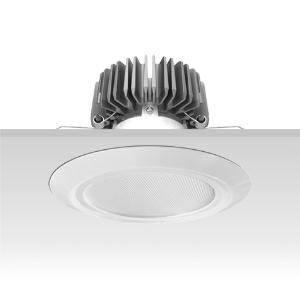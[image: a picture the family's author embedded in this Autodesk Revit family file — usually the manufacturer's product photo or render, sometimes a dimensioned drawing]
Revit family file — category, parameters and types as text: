
# Revit family: 3f_filippi_-_3f_reno_bianco_ampio_3f_filippi_-_30646_a01048_-_3f_reno_200_wh_2000-840_ep_wide___smp_wh_6cd9
name_source: partatom
category: Lighting Fixtures
units: mm (PartAtom-declared; Revit-internal decimal feet)

## family parameters
Cut with Voids When Loaded = No
Host = Face
Light Source = No
Part Type = Normal
Room Calculation Point = No
Round Connector Dimension = Use Diameter
Shared = No

## types (1)
- 3F Filippi - 3F Reno Bianco Ampio (1 x LED, 1723 lm, 21 W, 4000 K)
    Apparent Load = 21 VA
    Approval mark = ENEC
    CIE Flux Codes = 74 92 98 100 100
    Color Rendering = 80
    Color Temperature = 4000 K
    Control Gear = Electronic ballast
    Default Elevation = 1800 mm
    Description = ILLUMINOTECHNICAL
Luminous efficiency 100% (DLOR 100%, ULOR 0%).
Initial luminous flux of the luminaire 1723 lm.
Emergency luminaire luminous flux BLF 20%.
Direct symmetric wide distribution.
Installation Interdistance Transv.D = 1.06 x hu - Long.D = 1.04 x hu.
Average luminance <3000 cd/m² for radial angles >65°.
Tabular UGR (CIE 117 - 4H-8H; S=0.25H; 70/50/20): RUG 21.4 - 21.3.
Beam angle: 70° - 69°.
Luminous efficacy 82 lm/W.
Lifetime (L90/B10): 30000 h. (tq+25°C)
Lifetime (L85/B10): 50000 h. (tq+25°C)
Lifetime (L70/B10): 80000 h. (tq+25°C)
Sudden decreased luminous flux after 50000 hours: 0% (C0).
Photobiological safety in compliance with IEC/TR 62778: RG0 risk exempt, (IEC 62471).
In compliance with IEC/EN 62722-2-1 - IEC/EN 62717 standards.

SOURCE
Compact LED module 2000/840.
Energy efficiency class (UE 2019/2020 - UE 2019/2015): D.
CIE 13.3 Colour rendering index: CRI >80 (R9 <50%).
IES TM-30 Fidelity Index: Rf = 84 Rg = 95.
CCT nominal colour temperature 4000 K.
Colour initial tolerance (MacAdam): SDCM 3.
Zhaga Book 3 compliant.

MECHANICAL
Passive heat dissipator in die-casting aluminium, oversized, for optimum thermal management of the LED module.
Parabolic element with graduated/concentric rings in white polycarbonate.
Transparent external lens with glossy and satin differentiated surfaces, with a cooling and anti-insect system in methacrylate (PMMA).
Fastening spring clips in stainless steel.
Dimensions: diameter 226 mm, height 146 mm. Weight 1.475 kg.
IP44 protection degree for exposed part, IP20 for recessed part.
Mechanical strength to impacts IK05 (0.7 joule).
Glow-wire test resistance 650°C.

ELECTRICAL
Wiring on a separate unit.
Halogen Free electronic wiring 230V-50/60Hz, power factor 0.90, THD <25%, constant output current, SELV, class II, 1 driver.
Power of the luminaire 21 W.
CE - IEC 60598-1 - EN 60598-1.
EP maintained emergency wiring on board, 1h duration, 24h recharge; compliant with EN 60598-2-22, excluding high risk areas.
SAFE FLICKER: PstLM=<1 and SVM=<0.4 (IEC TR 61547-1 and IEC TR 63158), to ensure a more comfortable and safe light.
Ambient temperature from +5°C to +25°C.
Temperature class T6 max 85°C.
Relative humidity UR: <85%.

INSTALLATION
Pull-up recessed fitting.
False ceiling carving: 200 mm.
All accessories dedicated to this product are available on the Catalog and on our website www.3F-Filippi.com.

ACCESSORIES
A01048 - Anti-glare microprismatic SMP diffuser in methacrylate (PMMA), locked and in line with the trim, in white polycarbonate.

APPLICATIONS
Suitable product for food production plants (HACCP), IFS (Food Version 6), BRC (GSFS Food Version 7).
Environments: architectural, commercial, exhibition areas, transit areas, corridors, shops, display windows, service areas.
In false ceilings with narrow voids.

WARNING
Luminaire designed for disposal/recycling at end-of-life.
Replaceable (LED only) light source by a professional. Replaceable control gear by a professional.
    Height = 0 mm  [stored 0 ft]
    Lamp = 1 x LED
    Lamp Light Flux = 1723 lm
    Lamp Power = 21 W
    Lamp count = 1
    Length = 226 mm
    Lifetime = 50000 h
    Luminous efficacy = 82 lm/W
    Manufacturer = 3F Filippi
    ModVariant = No
    Model = 3F Filippi - 30646+A01048 - 3F Reno 200 WH 2000-840 EP WIDE + SMP WH
    Mounting Place = Ceiling
    Mounting Type = Recessed
    Number of Poles = 1
    OnlyDefault = Yes
    Power Factor = 1
    Product Name = 3F Filippi - 3F Reno Bianco Ampio
    Product group = recessed luminaire
    ProductGroupID = 4
    Protection Class = Protection class II
    Protection Degree = IP 20
    RLX_Detail_Level = 1
    RLX_Emergency_Light_Flux = 0 lm
    RLX_Emergency_Type = 0
    RLX_Emergency_Type_DB = No
    RlxData = <blob elided: 94529 chars, md5=ec0a489d>
    Socket = socket
    Standby Power = 0 W
    System Light Flux = 1723 lm
    System Power = 21 W
    Type Comments = Product without accessories
    Type Image = 3ffilippi_3f_reno_200_wh_vs_smp.jpg
    URL = http://relux.com
    VarID = ---
    Voltage = 0 V
    Weight = 0.00 kg
    Width = 0 mm  [stored 0 ft]

note: [stored X ft] marks values corroborated as IEEE doubles in the binary element streams (Revit-internal decimal feet)

## geometry (parser evidence)
native form markers: Blend x4, Sweep x11
no freeform markers — native parametric forms only
